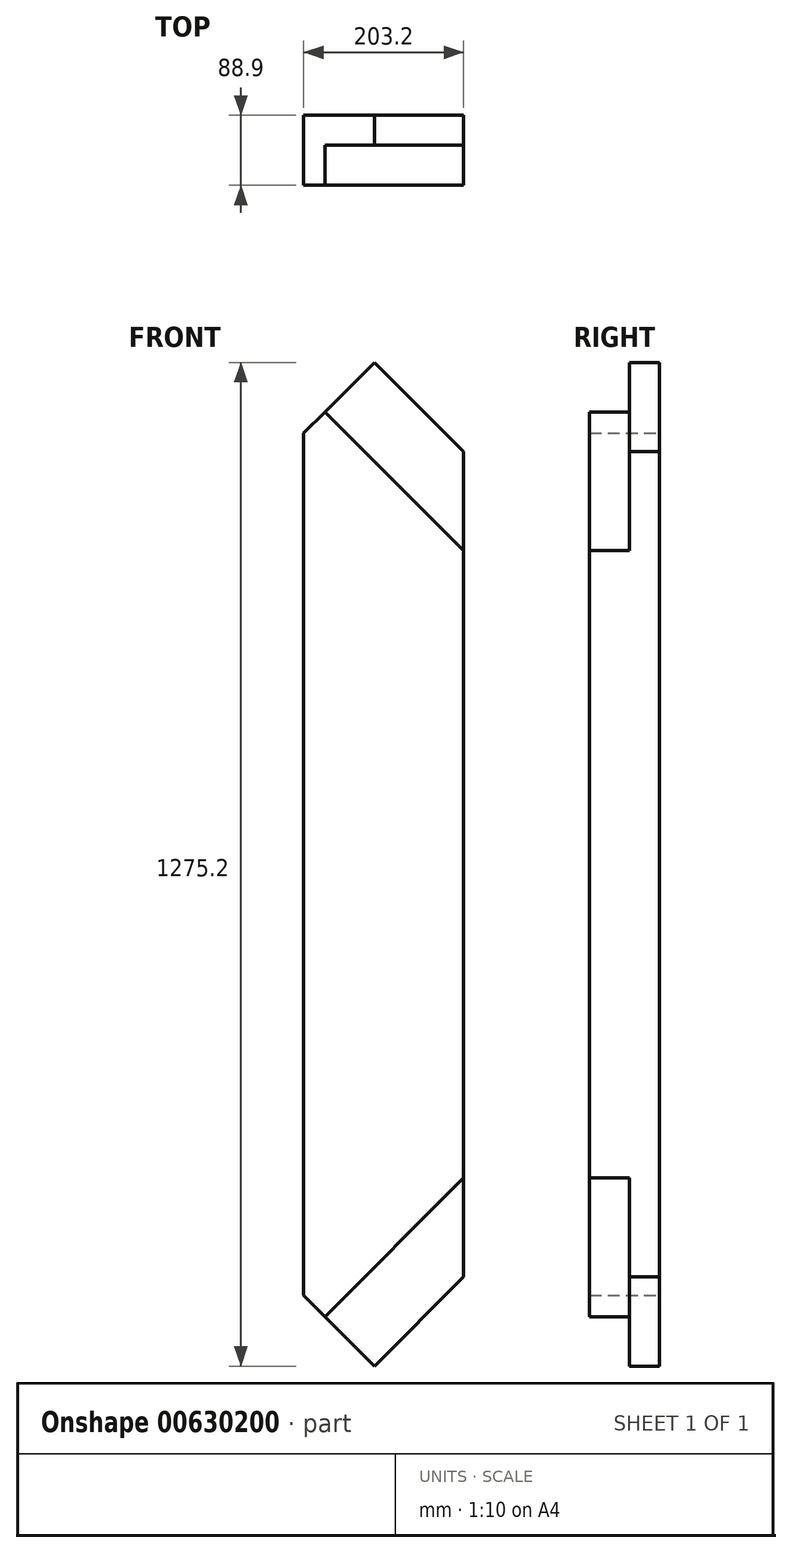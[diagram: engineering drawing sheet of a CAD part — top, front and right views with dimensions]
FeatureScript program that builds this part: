
annotation { "Feature Type Name" : "Feature", "Feature Type Description" : "" }
export const myFeature = defineFeature(function(context is Context, id is Id, definition is map)
    precondition{}
    {
        {
            var Q0;
            Q0=qCreatedBy(makeId("Front.planeOp"),FACE);
            var sketch = newSketch(context, id + "F0", { "sketchPlane" : qUnion([Q0])});
            skLineSegment(sketch, "E0.bottom", {"start": v(-101.6, 698.5) * mm, "end": v(101.6, 698.5) * mm});
            skLineSegment(sketch, "E0.top", {"start": v(-101.6, -698.5) * mm, "end": v(101.6, -698.5) * mm});
            skLineSegment(sketch, "E0.left", {"start": v(-101.6, 698.5) * mm, "end": v(-101.6, -698.5) * mm});
            skLineSegment(sketch, "E0.right", {"start": v(101.6, 698.5) * mm, "end": v(101.6, -698.5) * mm});
            skPoint(sketch, "E0.middle", {"position": v(0, 0) * mm});
            skLineSegment(sketch, "E1", {"start": v(-101.6, 543.35) * mm, "end": v(101.6, 340.15) * mm});
            skLineSegment(sketch, "E2", {"start": v(-101.6, 543.35) * mm, "end": v(-11.8, 633.15) * mm});
            skLineSegment(sketch, "E3", {"start": v(-11.8, 633.15) * mm, "end": v(101.6, 519.76) * mm});
            skLineSegment(sketch, "E4", {"start": v(-74.66, 570.3) * mm, "end": v(101.6, 394.03) * mm});
            skLineSegment(sketch, "E5", {"start": v(101.6, -349.04) * mm, "end": v(-101.6, -552.24) * mm});
            skLineSegment(sketch, "E6", {"start": v(-101.6, -552.24) * mm, "end": v(-11.8, -642.05) * mm});
            skLineSegment(sketch, "E7", {"start": v(-11.8, -642.05) * mm, "end": v(101.6, -528.65) * mm});
            skLineSegment(sketch, "E8", {"start": v(101.6, -402.93) * mm, "end": v(-74.66, -579.19) * mm});
            skSolve(sketch);
        }
        {
            var Q0;
            {var subQ0=sQuery(id+"F0.wireOp",EDGE,"E1");Q0=makeQuery(id+"F0.imprint","IMPRINT",FACE,{"disambiguationData":[TD([[makeQuery(id+"F0.imprint","IMPRINT",EDGE,{"derivedFrom":subQ0}),-1.0]])]});}
            var Q1;
            {var subQ0=sQuery(id+"F0.wireOp",EDGE,"E5");Q1=makeQuery(id+"F0.imprint","IMPRINT",FACE,{"disambiguationData":[TD([[makeQuery(id+"F0.imprint","IMPRINT",EDGE,{"derivedFrom":subQ0}),1.0]])]});}
            var Q2;
            {var subQ0=sQuery(id+"F0.wireOp",EDGE,"E1");Q2=makeQuery(id+"F0.imprint","IMPRINT",FACE,{"disambiguationData":[TD([[makeQuery(id+"F0.imprint","IMPRINT",EDGE,{"derivedFrom":subQ0}),1.0]])]});}
            extrude(context, id + "F1", {"entities" : qUnion([Q0, Q1, Q2]), "depth" : 88.9 * mm});
        }
        {
            var Q0;
            {var subQ0=sQuery(id+"F0.wireOp",EDGE,"E3");Q0=makeQuery(id+"F0.imprint","IMPRINT",FACE,{"disambiguationData":[TD([[makeQuery(id+"F0.imprint","IMPRINT",EDGE,{"derivedFrom":subQ0}),-1.0]])]});}
            var Q1;
            {var subQ0=sQuery(id+"F0.wireOp",EDGE,"E7");Q1=makeQuery(id+"F0.imprint","IMPRINT",FACE,{"disambiguationData":[TD([[makeQuery(id+"F0.imprint","IMPRINT",EDGE,{"derivedFrom":subQ0}),1.0]])]});}
            extrude(context, id + "F2", {"entities" : qUnion([Q0, Q1]), "operationType" : NewBodyOperationType.ADD, "depth" : 38.1 * mm});
        }
    });
